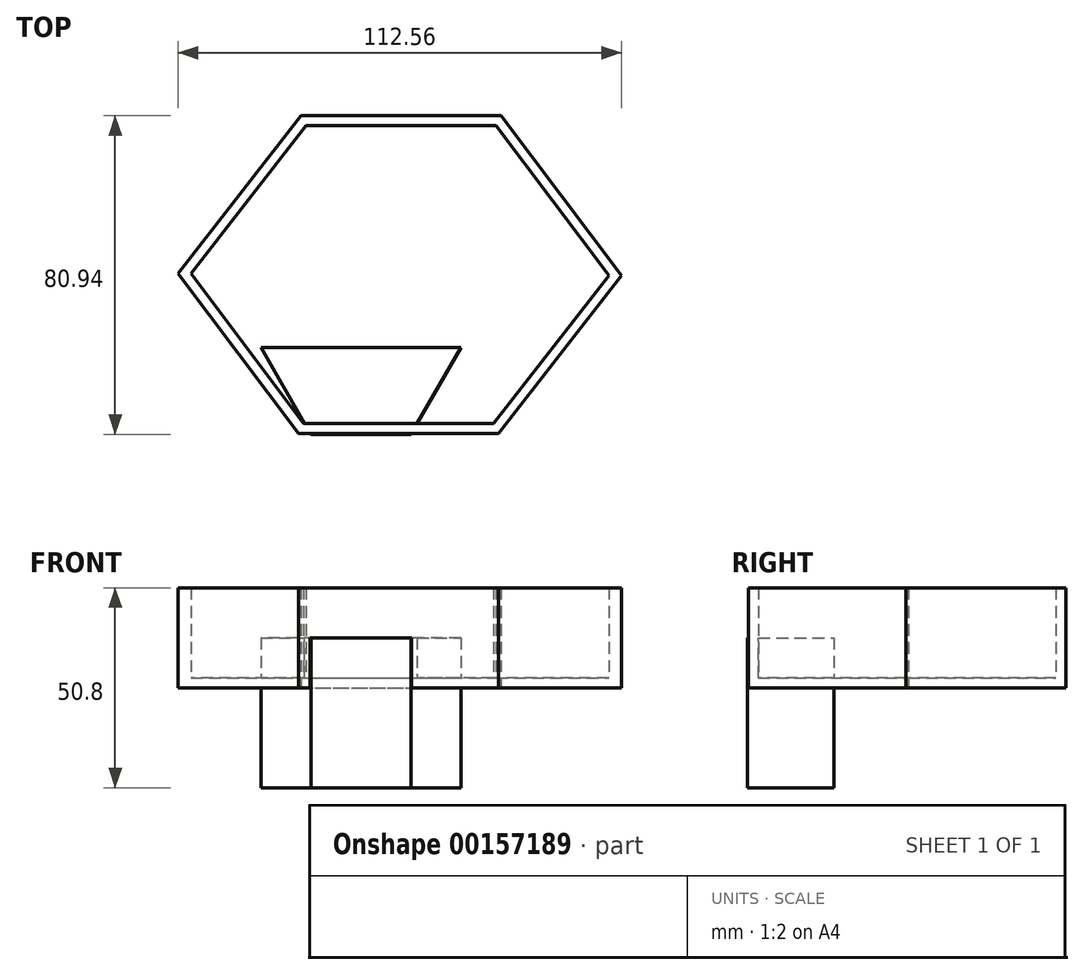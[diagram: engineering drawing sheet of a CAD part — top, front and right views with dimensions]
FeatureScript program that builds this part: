
annotation { "Feature Type Name" : "Feature", "Feature Type Description" : "" }
export const myFeature = defineFeature(function(context is Context, id is Id, definition is map)
    precondition{}
    {
        {
            var Q0;
            Q0=qCreatedBy(makeId("Top.planeOp"),FACE);
            var sketch = newSketch(context, id + "F0", { "sketchPlane" : qUnion([Q0])});
            skLineSegment(sketch, "E0", {"start": v(-40.54, 58.94) * mm, "end": v(10.26, 58.94) * mm});
            skLineSegment(sketch, "E1", {"start": v(10.26, 58.94) * mm, "end": v(40.79, 18.34) * mm});
            skLineSegment(sketch, "E2", {"start": v(40.79, 18.34) * mm, "end": v(9.56, -21.73) * mm});
            skLineSegment(sketch, "E3", {"start": v(9.56, -21.73) * mm, "end": v(-41.24, -21.73) * mm});
            skLineSegment(sketch, "E4", {"start": v(-41.24, -21.73) * mm, "end": v(-71.77, 18.87) * mm});
            skLineSegment(sketch, "E5", {"start": v(-71.77, 18.87) * mm, "end": v(-40.54, 58.94) * mm});
            skSolve(sketch);
        }
        {
            var Q0;
            Q0=qSketchRegion(id+"F0",true);
            extrude(context, id + "F1", {"entities" : qUnion([Q0]), "depth" : 25.4 * mm});
        }
        {
            var Q0;
            Q0=makeQuery(id+"F1.opExtrude","CAP_FACE",FACE,{"disambiguationData":[OSD([sQuery(id+"F0.wireOp",EDGE,"E0"),sQuery(id+"F0.wireOp",EDGE,"E1"),sQuery(id+"F0.wireOp",EDGE,"E2"),sQuery(id+"F0.wireOp",EDGE,"E3"),sQuery(id+"F0.wireOp",EDGE,"E4"),sQuery(id+"F0.wireOp",EDGE,"E5")])],"isStart":false});
            shell(context, id + "F2", {"entities" : qUnion([Q0]), "thickness" : 2.54 * mm});
        }
        {
            var Q0;
            Q0=qCreatedBy(makeId("Top.planeOp"),FACE);
            var sketch = newSketch(context, id + "F3", { "sketchPlane" : qUnion([Q0])});
            skLineSegment(sketch, "E6", {"start": v(-25.26, 47.57) * mm, "end": v(-17.64, 47.57) * mm});
            skLineSegment(sketch, "E7", {"start": v(-17.64, 47.57) * mm, "end": v(-11.8, 42.68) * mm});
            skLineSegment(sketch, "E8", {"start": v(-11.8, 42.68) * mm, "end": v(-16.69, 36.84) * mm});
            skLineSegment(sketch, "E9", {"start": v(-16.69, 36.84) * mm, "end": v(-24.3, 36.84) * mm});
            skLineSegment(sketch, "E10", {"start": v(-24.3, 36.84) * mm, "end": v(-30.15, 41.73) * mm});
            skLineSegment(sketch, "E11", {"start": v(-30.15, 41.73) * mm, "end": v(-25.26, 47.57) * mm});
            skSolve(sketch);
        }
        {
            var Q0;
            Q0=sQuery(id+"F3.wireOp",EDGE,"E10");
            var Q1;
            Q1=sQuery(id+"F3.wireOp",EDGE,"E11");
            var Q2;
            Q2=sQuery(id+"F3.wireOp",EDGE,"E6");
            var Q3;
            Q3=sQuery(id+"F3.wireOp",EDGE,"E7");
            var Q4;
            Q4=sQuery(id+"F3.wireOp",EDGE,"E8");
            var Q5;
            Q5=sQuery(id+"F3.wireOp",EDGE,"E9");
            extrude(context, id + "F4", {"bodyType" : ToolBodyType.SURFACE, "surfaceEntities" : qUnion([Q0, Q1, Q2, Q3, Q4, Q5]), "depth" : 12.7 * mm});
        }
        {
            var Q0;
            Q0=qCreatedBy(makeId("Top.planeOp"),FACE);
            var sketch = newSketch(context, id + "F5", { "sketchPlane" : qUnion([Q0])});
            skLineSegment(sketch, "E12", {"start": v(-27.25, 34.2) * mm, "end": v(-14.55, 34.2) * mm});
            skLineSegment(sketch, "E13", {"start": v(-14.55, 34.2) * mm, "end": v(-8.69, 29.33) * mm});
            skLineSegment(sketch, "E14", {"start": v(-8.69, 29.33) * mm, "end": v(-14.63, 24.56) * mm});
            skLineSegment(sketch, "E15", {"start": v(-14.63, 24.56) * mm, "end": v(-27.33, 24.56) * mm});
            skLineSegment(sketch, "E16", {"start": v(-27.33, 24.56) * mm, "end": v(-33.2, 29.43) * mm});
            skLineSegment(sketch, "E17", {"start": v(-33.2, 29.43) * mm, "end": v(-27.25, 34.2) * mm});
            skSolve(sketch);
        }
        {
            var Q0;
            Q0=sQuery(id+"F5.wireOp",EDGE,"E17");
            var Q1;
            Q1=sQuery(id+"F5.wireOp",EDGE,"E12");
            var Q2;
            Q2=sQuery(id+"F5.wireOp",EDGE,"E13");
            var Q3;
            Q3=sQuery(id+"F5.wireOp",EDGE,"E14");
            var Q4;
            Q4=sQuery(id+"F5.wireOp",EDGE,"E15");
            var Q5;
            Q5=sQuery(id+"F5.wireOp",EDGE,"E16");
            extrude(context, id + "F6", {"bodyType" : ToolBodyType.SURFACE, "surfaceEntities" : qUnion([Q0, Q1, Q2, Q3, Q4, Q5]), "depth" : 12.7 * mm});
        }
        {
            var Q0;
            Q0=qCreatedBy(makeId("Top.planeOp"),FACE);
            var sketch = newSketch(context, id + "F7", { "sketchPlane" : qUnion([Q0])});
            skLineSegment(sketch, "E18", {"start": v(-50.8, 0) * mm, "end": v(-38.1, -22) * mm});
            skLineSegment(sketch, "E19", {"start": v(-38.1, -22) * mm, "end": v(-12.7, -22) * mm});
            skLineSegment(sketch, "E20", {"start": v(-12.7, -22) * mm, "end": v(0, 0) * mm});
            skLineSegment(sketch, "E21", {"start": v(0, 0) * mm, "end": v(-50.8, 0) * mm});
            skSolve(sketch);
        }
        {
            var Q0;
            Q0=qSketchRegion(id+"F7",true);
            extrude(context, id + "F8", {"entities" : qUnion([Q0]), "operationType" : NewBodyOperationType.ADD, "depth" : 12.7 * mm, "hasSecondDirection" : true, "secondDirectionOppositeDirection" : true, "secondDirectionDepth" : 25.4 * mm});
        }
    });
